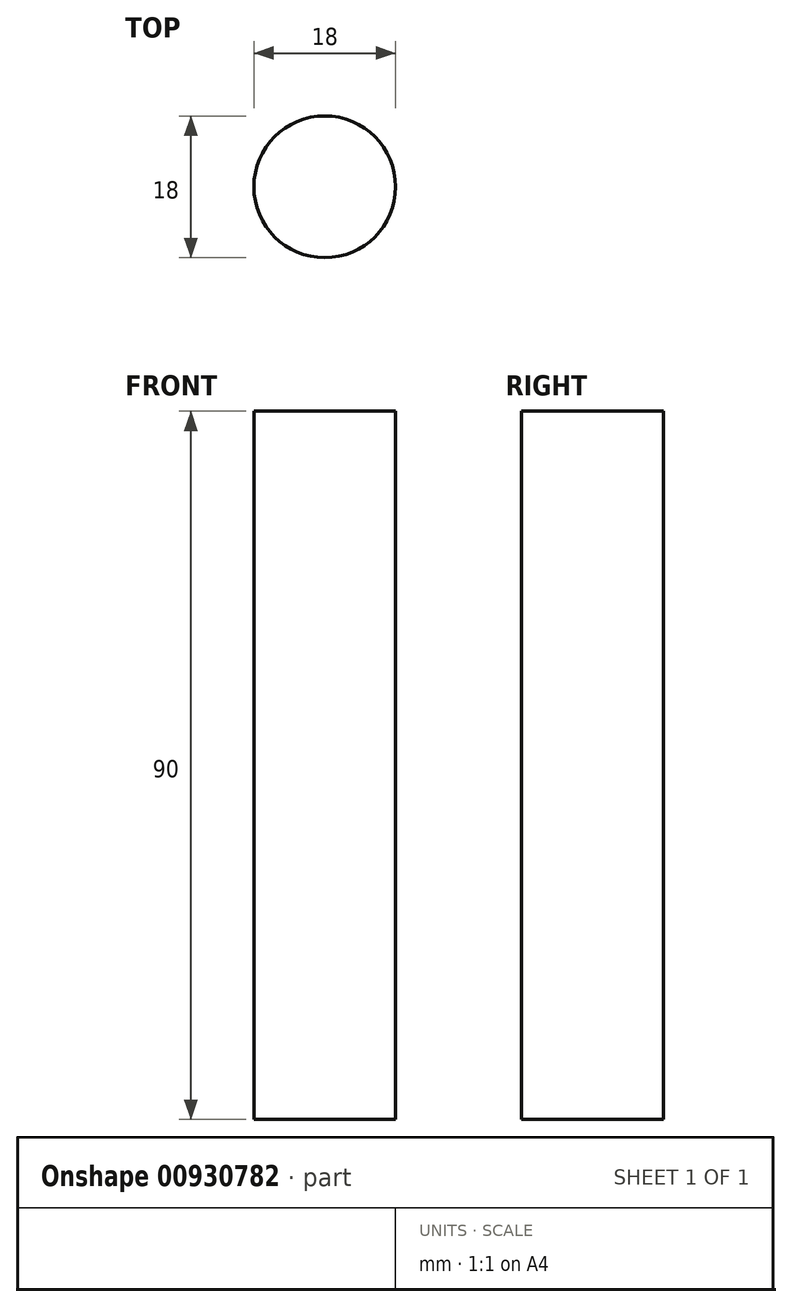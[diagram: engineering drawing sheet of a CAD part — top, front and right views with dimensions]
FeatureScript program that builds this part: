
annotation { "Feature Type Name" : "Feature", "Feature Type Description" : "" }
export const myFeature = defineFeature(function(context is Context, id is Id, definition is map)
    precondition{}
    {
        {
            var Q0;
            Q0=qCreatedBy(makeId("Top.planeOp"),FACE);
            var sketch = newSketch(context, id + "F0", { "sketchPlane" : qUnion([Q0])});
            skCircle(sketch, "E0", {"center": v(0, 0) * mm, "radius": 9 * mm});
            skSolve(sketch);
        }
        {
            var Q0;
            Q0=makeQuery(id+"F0.imprint","IMPRINT",FACE,{"disambiguationData":[TD([[makeQuery(id+"F0.imprint","IMPRINT",EDGE,{"derivedFrom":sQuery(id+"F0.wireOp",EDGE,"E0")}),1.0]])]});
            extrude(context, id + "F1", {"entities" : qUnion([Q0]), "depth" : 90 * mm, "offsetDistance" : 25 * mm});
        }
    });
